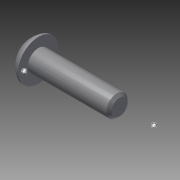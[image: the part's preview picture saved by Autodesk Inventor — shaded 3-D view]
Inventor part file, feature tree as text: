
AUTODESK INVENTOR PART (.ipt)
format: ipt  version: 2015 (Build 190159000, 159)  size: 124,416 bytes
history: native  units: in
note: dims shown in document units (in); Inventor stores cm internally (conversion verified against a paired STEP export)
features: other x3, extrude x1, chamfer x1, imported_body x1, sketch x1
ambient origin geometry x8: Origin, YZ Plane, XZ Plane, XY Plane, X Axis, Y Axis, Z Axis, Center Point
bodies: Body1 (feature_tree)
feature tree (7):
  other  "Bolt 0.625 inch"
  parser-record x1  (decoder bookkeeping rows leaked as tree rows — omitted from the tree; the rows remain in map.json)
  other  "Bolt"
  extrude  "thread length"  Depth=0.625in TaperAngle=0.0deg
  chamfer  "thread chamfer"  Distance=0.02in Angle=45.0deg
  imported_body  "Base1"
  sketch  "Sketch1"  dims[d0=0.164in d1=0.625in d2=0.0in d3=0.02in d4=0.125in d5=45.0deg d7=0.0in d9=0.0in]
